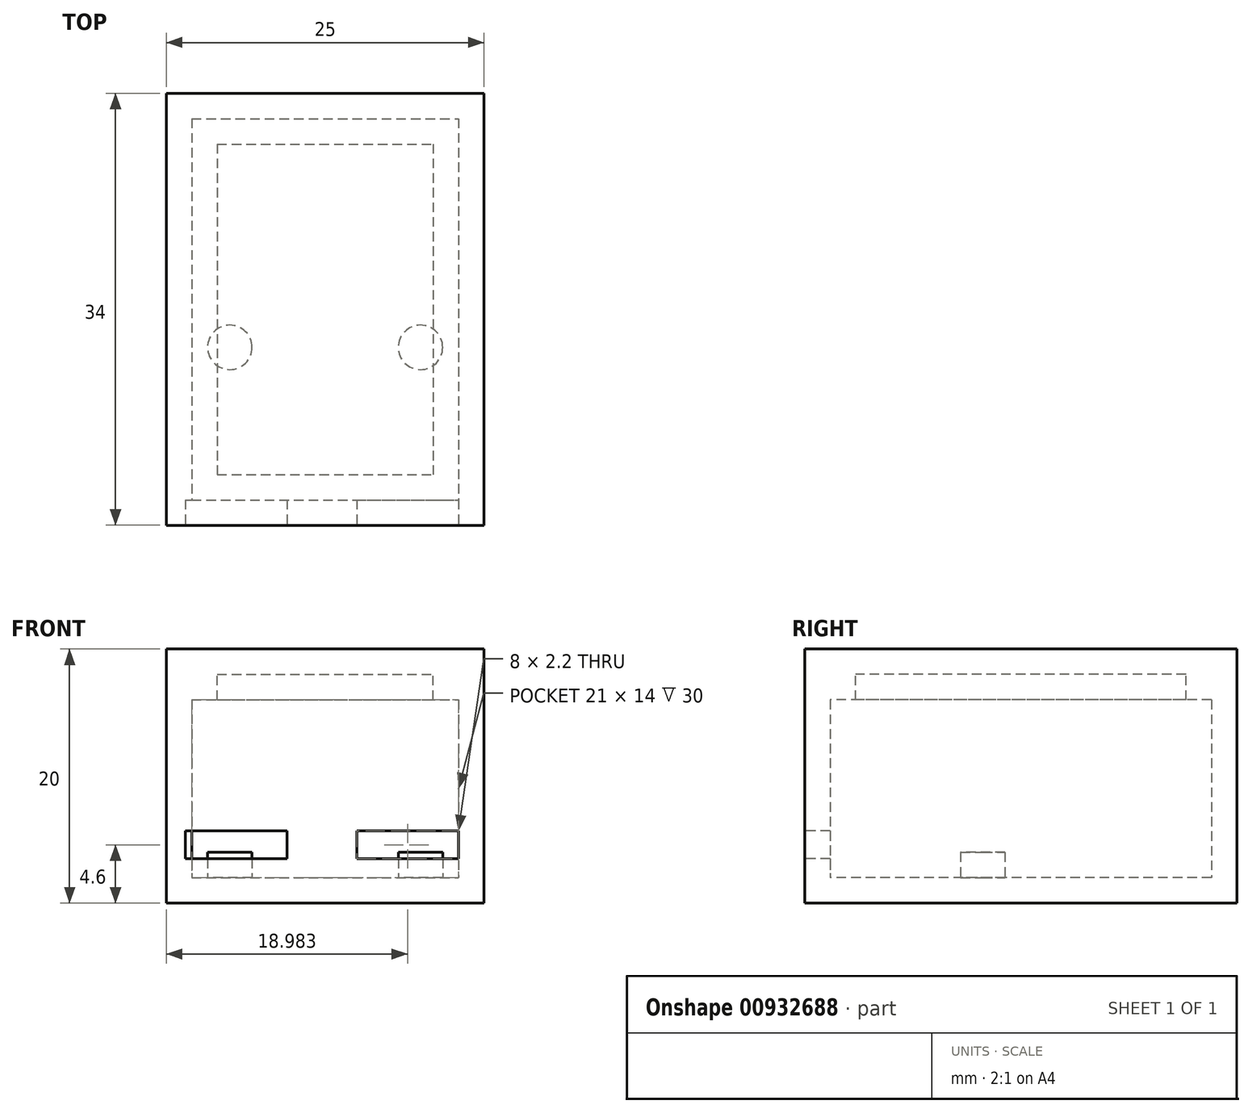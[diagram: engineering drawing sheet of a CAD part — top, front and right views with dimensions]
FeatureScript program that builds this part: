
annotation { "Feature Type Name" : "Feature", "Feature Type Description" : "" }
export const myFeature = defineFeature(function(context is Context, id is Id, definition is map)
    precondition{}
    {
        {
            var Q0;
            Q0=qCreatedBy(makeId("Top.planeOp"),FACE);
            var sketch = newSketch(context, id + "F0", { "sketchPlane" : qUnion([Q0])});
            skLineSegment(sketch, "E0.bottom", {"start": v(-54, 31.4) * mm, "end": v(-29, 31.4) * mm});
            skLineSegment(sketch, "E0.top", {"start": v(-54, -2.6) * mm, "end": v(-29, -2.6) * mm});
            skLineSegment(sketch, "E0.left", {"start": v(-54, 31.4) * mm, "end": v(-54, -2.6) * mm});
            skLineSegment(sketch, "E0.right", {"start": v(-29, 31.4) * mm, "end": v(-29, -2.6) * mm});
            skSolve(sketch);
        }
        {
            var Q0;
            Q0=makeQuery(id+"F0.imprint","IMPRINT",FACE,{"disambiguationData":[TD([[makeQuery(id+"F0.imprint","IMPRINT",EDGE,{"derivedFrom":sQuery(id+"F0.wireOp",EDGE,"E0.bottom")}),-1.0]])]});
            extrude(context, id + "F1", {"entities" : qUnion([Q0]), "oppositeDirection" : true, "depth" : 2 * mm, "offsetDistance" : 25 * mm});
        }
        {
            var Q0;
            Q0=makeQuery(id+"F1.opExtrude","CAP_FACE",FACE,{"disambiguationData":[OSD([sQuery(id+"F0.wireOp",EDGE,"E0.bottom"),sQuery(id+"F0.wireOp",EDGE,"E0.top"),sQuery(id+"F0.wireOp",EDGE,"E0.left"),sQuery(id+"F0.wireOp",EDGE,"E0.right")])],"isStart":true});
            var sketch = newSketch(context, id + "F2", { "sketchPlane" : qUnion([Q0])});
            skLineSegment(sketch, "E1.bottom", {"start": v(-52, 29.4) * mm, "end": v(-31, 29.4) * mm});
            skLineSegment(sketch, "E1.top", {"start": v(-52, -0.6) * mm, "end": v(-31, -0.6) * mm});
            skLineSegment(sketch, "E1.left", {"start": v(-52, 29.4) * mm, "end": v(-52, -0.6) * mm});
            skLineSegment(sketch, "E1.right", {"start": v(-31, 29.4) * mm, "end": v(-31, -0.6) * mm});
            skSolve(sketch);
        }
        {
            var Q0;
            Q0=makeQuery(id+"F2.imprint","IMPRINT",FACE,{"disambiguationData":[TD([[makeQuery(id+"F2.imprint","IMPRINT",EDGE,{"derivedFrom":sQuery(id+"F2.wireOp",EDGE,"E1.bottom")}),1.0]])]});
            extrude(context, id + "F3", {"entities" : qUnion([Q0]), "operationType" : NewBodyOperationType.ADD, "depth" : 16 * mm, "offsetDistance" : 25 * mm});
        }
        {
            var Q0;
            {var subQ0=sQuery(id+"F0.wireOp",EDGE,"E0.top");Q0=makeQuery(id+"F3.boolean.opBoolean","MERGE",FACE,{"derivedFrom":[makeQuery(id+"F1.opExtrude","SWEPT_FACE",FACE,{"disambiguationData":[OSD([subQ0])]}),makeQuery(id+"F3.opExtrude","SWEPT_FACE",FACE,{"disambiguationData":[OSD([subQ0])]})]});}
            var sketch = newSketch(context, id + "F4", { "sketchPlane" : qUnion([Q0])});
            skLineSegment(sketch, "E2.bottom", {"start": v(-52.5, 1.5) * mm, "end": v(-44.5, 1.5) * mm});
            skLineSegment(sketch, "E2.top", {"start": v(-52.5, 3.7) * mm, "end": v(-44.5, 3.7) * mm});
            skLineSegment(sketch, "E2.left", {"start": v(-52.5, 1.5) * mm, "end": v(-52.5, 3.7) * mm});
            skLineSegment(sketch, "E2.right", {"start": v(-44.5, 1.5) * mm, "end": v(-44.5, 3.7) * mm});
            skPoint(sketch, "E3.firstSnap0", {"position": v(-48.5, 3.7) * mm});
            skLineSegment(sketch, "E3.bottom", {"start": v(-39, 3.7) * mm, "end": v(-31, 3.7) * mm});
            skLineSegment(sketch, "E3.top", {"start": v(-39, 1.5) * mm, "end": v(-31, 1.5) * mm});
            skLineSegment(sketch, "E3.left", {"start": v(-39, 3.7) * mm, "end": v(-39, 1.5) * mm});
            skLineSegment(sketch, "E3.right", {"start": v(-31, 3.7) * mm, "end": v(-31, 1.5) * mm});
            skSolve(sketch);
        }
        {
            var Q0;
            Q0=makeQuery(id+"F4.imprint","IMPRINT",FACE,{"disambiguationData":[TD([[makeQuery(id+"F4.imprint","IMPRINT",EDGE,{"derivedFrom":sQuery(id+"F4.wireOp",EDGE,"E2.bottom")}),1.0]])]});
            var Q1;
            Q1=makeQuery(id+"F4.imprint","IMPRINT",FACE,{"disambiguationData":[TD([[makeQuery(id+"F4.imprint","IMPRINT",EDGE,{"derivedFrom":sQuery(id+"F4.wireOp",EDGE,"E3.bottom")}),-1.0]])]});
            extrude(context, id + "F5", {"entities" : qUnion([Q0, Q1]), "operationType" : NewBodyOperationType.REMOVE, "oppositeDirection" : true, "depth" : 2 * mm, "offsetDistance" : 25 * mm});
        }
        {
            var Q0;
            Q0=makeQuery(id+"F1.opExtrude","CAP_FACE",FACE,{"disambiguationData":[OSD([sQuery(id+"F0.wireOp",EDGE,"E0.bottom"),sQuery(id+"F0.wireOp",EDGE,"E0.top"),sQuery(id+"F0.wireOp",EDGE,"E0.left"),sQuery(id+"F0.wireOp",EDGE,"E0.right")])],"isStart":true});
            var sketch = newSketch(context, id + "F6", { "sketchPlane" : qUnion([Q0])});
            skCircle(sketch, "E4", {"center": v(-34, 11.4) * mm, "radius": 1.75 * mm});
            skCircle(sketch, "E5", {"center": v(-49, 11.4) * mm, "radius": 1.75 * mm});
            skSolve(sketch);
        }
        {
            var Q0;
            Q0=makeQuery(id+"F6.imprint","IMPRINT",FACE,{"disambiguationData":[TD([[makeQuery(id+"F6.imprint","IMPRINT",EDGE,{"derivedFrom":sQuery(id+"F6.wireOp",EDGE,"E5")}),1.0]])]});
            var Q1;
            Q1=makeQuery(id+"F6.imprint","IMPRINT",FACE,{"disambiguationData":[TD([[makeQuery(id+"F6.imprint","IMPRINT",EDGE,{"derivedFrom":sQuery(id+"F6.wireOp",EDGE,"E4")}),1.0]])]});
            extrude(context, id + "F7", {"entities" : qUnion([Q0, Q1]), "operationType" : NewBodyOperationType.ADD, "depth" : 2 * mm, "offsetDistance" : 25 * mm});
        }
        {
            var Q0;
            Q0=makeQuery(id+"F3.opExtrude","CAP_FACE",FACE,{"disambiguationData":[OSD([sQuery(id+"F0.wireOp",EDGE,"E0.bottom"),sQuery(id+"F0.wireOp",EDGE,"E0.top"),sQuery(id+"F0.wireOp",EDGE,"E0.left"),sQuery(id+"F0.wireOp",EDGE,"E0.right"),sQuery(id+"F2.wireOp",EDGE,"E1.bottom"),sQuery(id+"F2.wireOp",EDGE,"E1.top"),sQuery(id+"F2.wireOp",EDGE,"E1.left"),sQuery(id+"F2.wireOp",EDGE,"E1.right")])],"isStart":false});
            var sketch = newSketch(context, id + "F8", { "sketchPlane" : qUnion([Q0])});
            skLineSegment(sketch, "E6.bottom", {"start": v(-54, 31.4) * mm, "end": v(-29, 31.4) * mm});
            skLineSegment(sketch, "E6.top", {"start": v(-54, -2.6) * mm, "end": v(-29, -2.6) * mm});
            skLineSegment(sketch, "E6.left", {"start": v(-54, 31.4) * mm, "end": v(-54, -2.6) * mm});
            skLineSegment(sketch, "E6.right", {"start": v(-29, 31.4) * mm, "end": v(-29, -2.6) * mm});
            skSolve(sketch);
        }
        {
            var Q0;
            Q0=makeQuery(id+"F8.imprint","IMPRINT",FACE,{"disambiguationData":[TD([[makeQuery(id+"F8.imprint","IMPRINT",EDGE,{"derivedFrom":sQuery(id+"F8.wireOp",EDGE,"E6.bottom")}),-1.0]])]});
            var Q1;
            Q1=makeQuery(id+"F8.imprint","IMPRINT",FACE,{"disambiguationData":[TD([[makeQuery(id+"F8.imprint","IMPRINT",EDGE,{"derivedFrom":makeQuery(id+"F3.opExtrude","CAP_EDGE",EDGE,{"disambiguationData":[OSD([sQuery(id+"F2.wireOp",EDGE,"E1.bottom")])],"isStart":false})}),-1.0]])]});
            extrude(context, id + "F9", {"entities" : qUnion([Q0, Q1]), "depth" : 2 * mm, "offsetDistance" : 25 * mm});
        }
        {
            var Q0;
            Q0=makeQuery(id+"F9.opExtrude","CAP_FACE",FACE,{"disambiguationData":[OSD([sQuery(id+"F8.wireOp",EDGE,"E6.bottom"),sQuery(id+"F8.wireOp",EDGE,"E6.top"),sQuery(id+"F8.wireOp",EDGE,"E6.left"),sQuery(id+"F8.wireOp",EDGE,"E6.right")])],"isStart":false});
            var sketch = newSketch(context, id + "F10", { "sketchPlane" : qUnion([Q0])});
            skLineSegment(sketch, "E7.bottom", {"start": v(-50, 27.4) * mm, "end": v(-33, 27.4) * mm});
            skLineSegment(sketch, "E7.top", {"start": v(-50, 1.4) * mm, "end": v(-33, 1.4) * mm});
            skLineSegment(sketch, "E7.left", {"start": v(-50, 27.4) * mm, "end": v(-50, 1.4) * mm});
            skLineSegment(sketch, "E7.right", {"start": v(-33, 27.4) * mm, "end": v(-33, 1.4) * mm});
            skLineSegment(sketch, "E8.bottom", {"start": v(-52, 29.4) * mm, "end": v(-31, 29.4) * mm});
            skLineSegment(sketch, "E8.top", {"start": v(-52, -0.6) * mm, "end": v(-31, -0.6) * mm});
            skLineSegment(sketch, "E8.left", {"start": v(-52, 29.4) * mm, "end": v(-52, -0.6) * mm});
            skLineSegment(sketch, "E8.right", {"start": v(-31, 29.4) * mm, "end": v(-31, -0.6) * mm});
            skSolve(sketch);
        }
        {
            var Q0;
            Q0=makeQuery(id+"F10.imprint","IMPRINT",FACE,{"disambiguationData":[TD([[makeQuery(id+"F10.imprint","IMPRINT",EDGE,{"derivedFrom":sQuery(id+"F10.wireOp",EDGE,"E7.bottom")}),1.0]])]});
            extrude(context, id + "F11", {"entities" : qUnion([Q0]), "operationType" : NewBodyOperationType.ADD, "oppositeDirection" : true, "depth" : 4 * mm, "offsetDistance" : 25 * mm});
        }
    });
